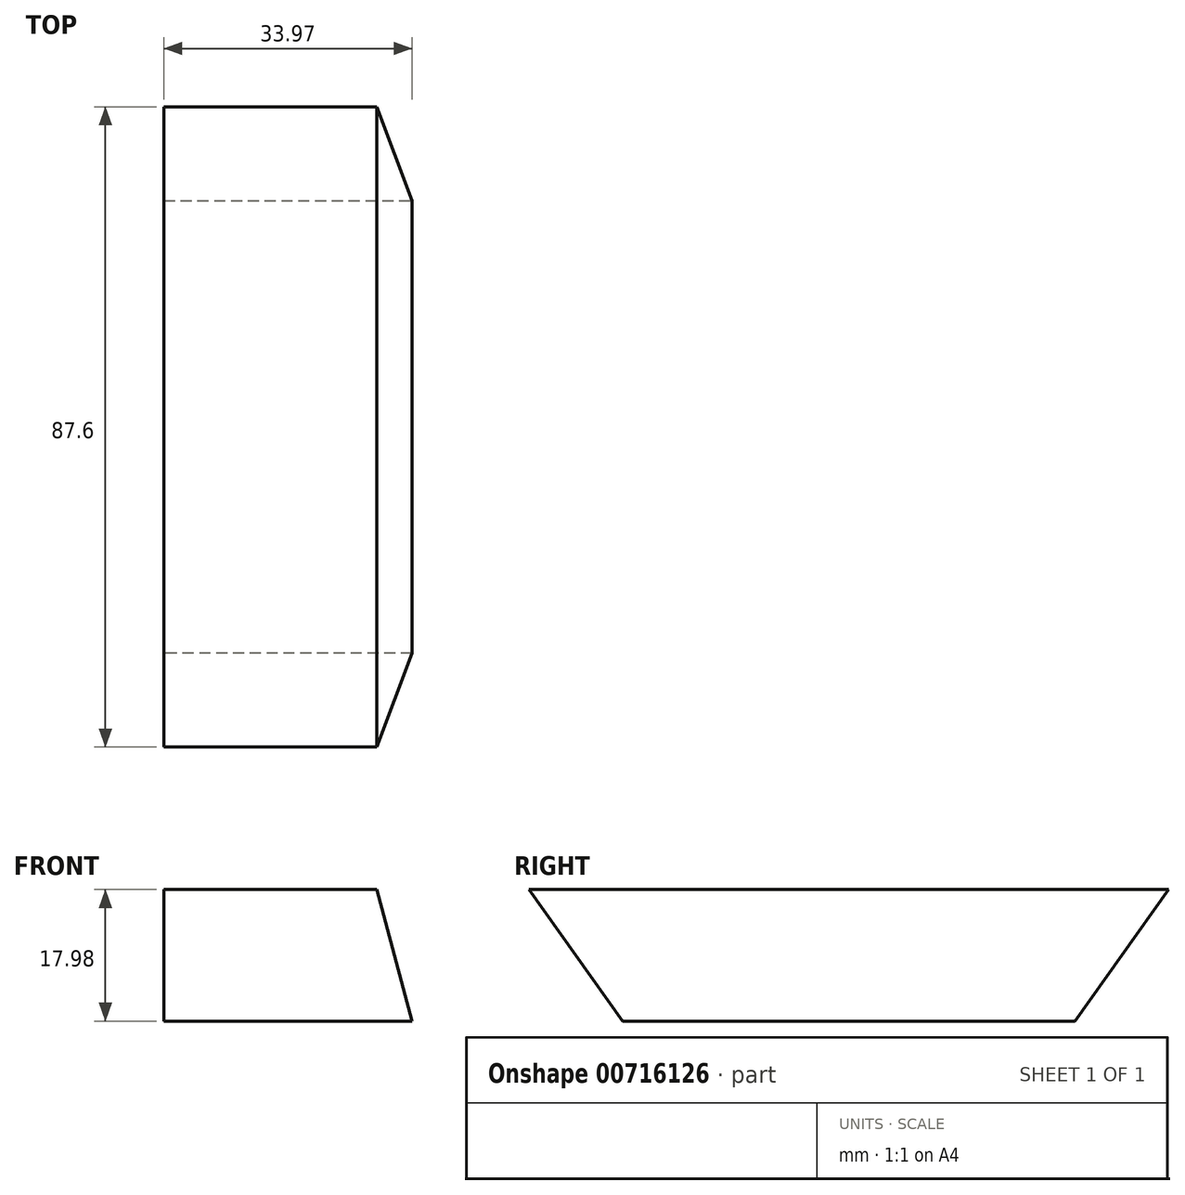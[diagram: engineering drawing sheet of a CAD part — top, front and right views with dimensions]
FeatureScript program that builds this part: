
annotation { "Feature Type Name" : "Feature", "Feature Type Description" : "" }
export const myFeature = defineFeature(function(context is Context, id is Id, definition is map)
    precondition{}
    {
        {
            var Q0;
            Q0=qCreatedBy(makeId("Top.planeOp"),FACE);
            var sketch = newSketch(context, id + "F0", { "sketchPlane" : qUnion([Q0])});
            skLineSegment(sketch, "E0.bottom", {"start": v(16.99, -43.95) * mm, "end": v(-16.99, -43.95) * mm});
            skLineSegment(sketch, "E0.top", {"start": v(16.99, 43.95) * mm, "end": v(-16.99, 43.95) * mm});
            skLineSegment(sketch, "E0.left", {"start": v(16.99, -43.95) * mm, "end": v(16.99, 43.95) * mm});
            skLineSegment(sketch, "E0.right", {"start": v(-16.99, -43.95) * mm, "end": v(-16.99, 43.95) * mm});
            skPoint(sketch, "E0.middle", {"position": v(0, 0) * mm});
            skSolve(sketch);
        }
        {
            var Q0;
            Q0=makeQuery(id+"F0.imprint","IMPRINT",FACE,{"disambiguationData":[TD([[makeQuery(id+"F0.imprint","IMPRINT",EDGE,{"derivedFrom":sQuery(id+"F0.wireOp",EDGE,"E0.bottom")}),-1.0]])]});
            extrude(context, id + "F1", {"entities" : qUnion([Q0]), "oppositeDirection" : true, "depth" : 17.98 * mm, "offsetDistance" : 25.4 * mm});
        }
        {
            var Q0;
            Q0=makeQuery(id+"F1.opExtrude","CAP_EDGE",EDGE,{"disambiguationData":[OSD([sQuery(id+"F0.wireOp",EDGE,"E0.bottom")])],"isStart":false});
            var Q1;
            Q1=makeQuery(id+"F1.opExtrude","CAP_EDGE",EDGE,{"disambiguationData":[OSD([sQuery(id+"F0.wireOp",EDGE,"E0.top")])],"isStart":false});
            chamfer(context, id + "F2", {"entities" : qUnion([Q0, Q1]), "chamferType" : ChamferType.OFFSET_ANGLE, "width" : 12.98 * mm, "oppositeDirection" : false, "angle" : 54.5 * degree, "tangentPropagation" : true});
        }
        {
            var Q0;
            Q0=makeQuery(id+"F1.opExtrude","CAP_EDGE",EDGE,{"disambiguationData":[OSD([sQuery(id+"F0.wireOp",EDGE,"E0.left")])],"isStart":true});
            chamfer(context, id + "F3", {"entities" : qUnion([Q0]), "chamferType" : ChamferType.OFFSET_ANGLE, "width" : 4.83 * mm, "oppositeDirection" : false, "angle" : 75 * degree, "tangentPropagation" : true});
        }
    });
